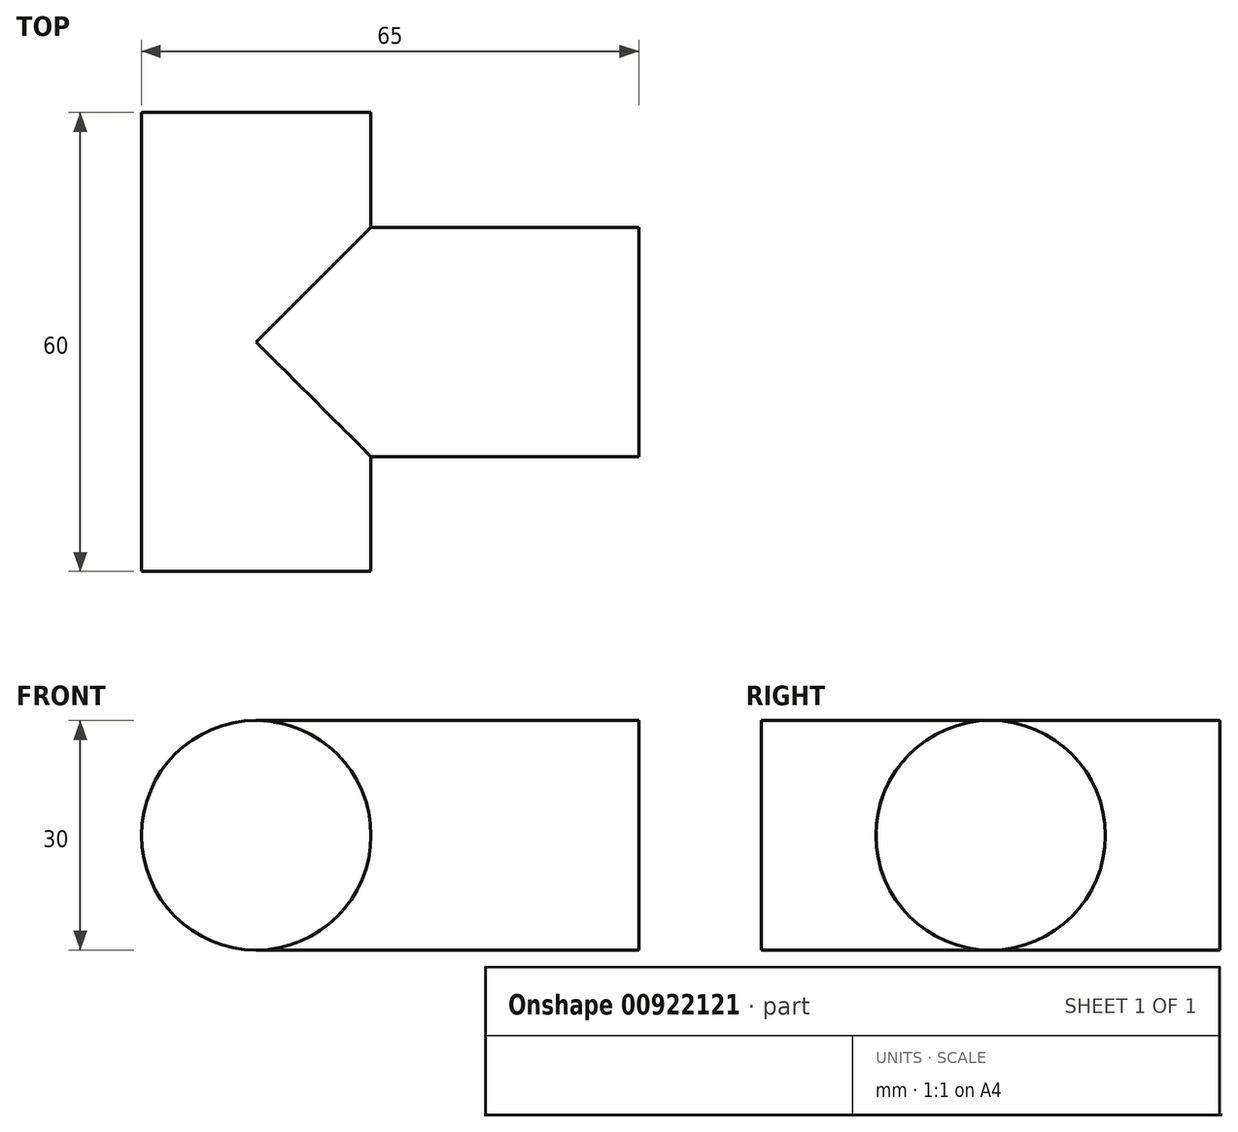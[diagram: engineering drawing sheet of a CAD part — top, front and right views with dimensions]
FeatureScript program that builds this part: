
annotation { "Feature Type Name" : "Feature", "Feature Type Description" : "" }
export const myFeature = defineFeature(function(context is Context, id is Id, definition is map)
    precondition{}
    {
        {
            var Q0;
            Q0=qCreatedBy(makeId("Front.planeOp"),FACE);
            var sketch = newSketch(context, id + "F0", { "sketchPlane" : qUnion([Q0])});
            skCircle(sketch, "E0", {"center": v(0, 0) * mm, "radius": 15 * mm});
            skSolve(sketch);
        }
        {
            var Q0;
            Q0=makeQuery(id+"F0.imprint","IMPRINT",FACE,{"disambiguationData":[TD([[makeQuery(id+"F0.imprint","IMPRINT",EDGE,{"derivedFrom":sQuery(id+"F0.wireOp",EDGE,"E0")}),1.0]])]});
            extrude(context, id + "F1", {"entities" : qUnion([Q0]), "endBound" : BoundingType.SYMMETRIC, "depth" : 60 * mm, "offsetDistance" : 25 * mm});
        }
        {
            var Q0;
            Q0=qCreatedBy(makeId("Right.planeOp"),FACE);
            var sketch = newSketch(context, id + "F2", { "sketchPlane" : qUnion([Q0])});
            skCircle(sketch, "E1", {"center": v(0, 0) * mm, "radius": 15 * mm});
            skSolve(sketch);
        }
        {
            var Q0;
            Q0 = qSketchRegion(id + "F2", true);
            extrude(context, id + "F3", {"entities" : qUnion([Q0]), "operationType" : NewBodyOperationType.ADD, "depth" : 50 * mm, "offsetDistance" : 25 * mm});
        }
    });
